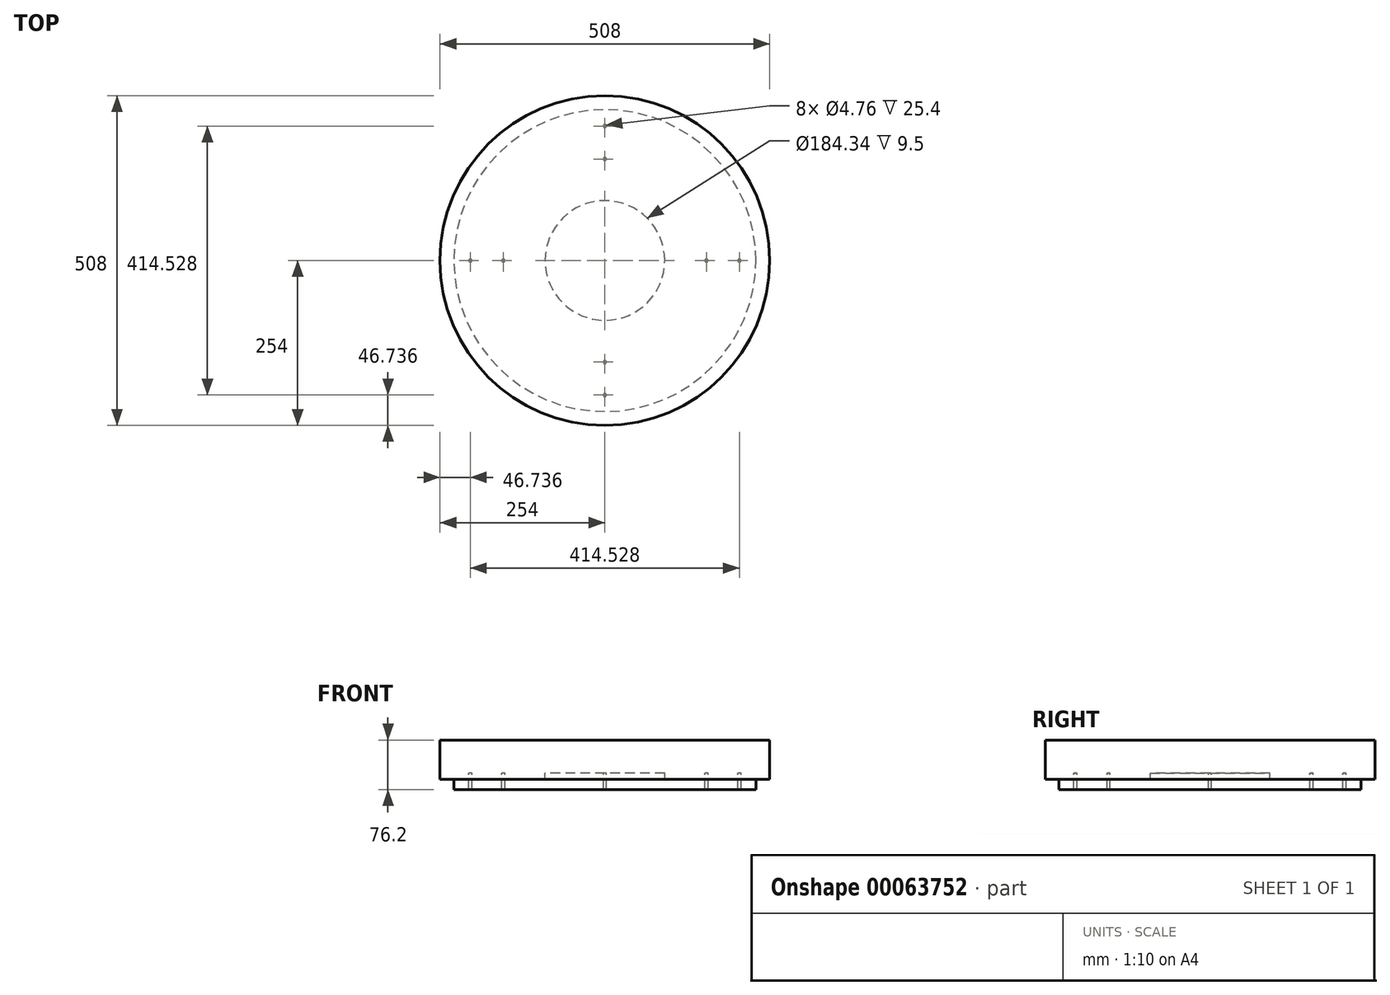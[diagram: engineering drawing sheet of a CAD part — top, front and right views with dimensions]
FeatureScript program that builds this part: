
annotation { "Feature Type Name" : "Feature", "Feature Type Description" : "" }
export const myFeature = defineFeature(function(context is Context, id is Id, definition is map)
    precondition{}
    {
        {
            assignVariable(context, id + "F0", {"name" : "H", "anyValue" : 15});
        }
        {
            assignVariable(context, id + "F1", {"name" : "S", "anyValue" : 4});
        }
        {
            var Q0;
            Q0=qCreatedBy(makeId("Top.planeOp"),FACE);
            var sketch = newSketch(context, id + "F2", { "sketchPlane" : qUnion([Q0])});
            skCircle(sketch, "E0", {"center": v(0, 0) * mm, "radius": 254 * mm});
            skCircle(sketch, "E1", {"center": v(0, 0) * mm, "radius": 241.3 * mm});
            skCircle(sketch, "E2.0", {"center": v(0, 0) * mm, "radius": 232.66 * mm});
            skSolve(sketch);
        }
        {
            var Q0;
            Q0=makeQuery(id+"F2.imprint","IMPRINT",FACE,{"disambiguationData":[TD([[makeQuery(id+"F2.imprint","IMPRINT",EDGE,{"derivedFrom":sQuery(id+"F2.wireOp",EDGE,"E1")}),1.0]])]});
            var Q1;
            Q1=sQuery(id+"F2.wireOp",EDGE,"E1");
            var Q2;
            Q2=sQuery(id+"F2.wireOp",EDGE,"E2.0");
            extrude(context, id + "F3", {"entities" : qUnion([Q0]), "surfaceEntities" : qUnion([Q1, Q2]), "depth" : (getVariable(context, 'H') - 5.5) * mm});
        }
        {
            var Q0;
            Q0=makeQuery(id+"F3.opExtrude","CAP_FACE",FACE,{"disambiguationData":[OSD([sQuery(id+"F2.wireOp",EDGE,"E1"),sQuery(id+"F2.wireOp",EDGE,"E2.0")])],"isStart":false});
            var sketch = newSketch(context, id + "F4", { "sketchPlane" : qUnion([Q0])});
            skCircle(sketch, "E3.0", {"center": v(0, 0) * mm, "radius": 232.66 * mm});
            skSolve(sketch);
        }
        {
            var Q0;
            Q0=qSketchRegion(id+"F4",true);
            extrude(context, id + "F5", {"entities" : qUnion([Q0]), "oppositeDirection" : true, "depth" : 25.4 * mm});
        }
        {
            var Q0;
            Q0=makeQuery(id+"F5.opExtrude","CAP_FACE",FACE,{"disambiguationData":[OSD([sQuery(id+"F4.wireOp",EDGE,"E3.0")])],"isStart":true});
            var sketch = newSketch(context, id + "F6", { "sketchPlane" : qUnion([Q0])});
            skLineSegment(sketch, "E4", {"start": v(-232.66, 0) * mm, "end": v(0, 0) * mm, "construction": true});
            skCircle(sketch, "E5.0", {"center": v(0, 0) * mm, "radius": 207.26 * mm, "construction": true});
            skCircle(sketch, "E6.0", {"center": v(0, 0) * mm, "radius": 156.46 * mm, "construction": true});
            skPoint(sketch, "E7", {"position": v(-207.26, 0) * mm});
            skPoint(sketch, "E8", {"position": v(-156.46, 0) * mm});
            skPoint(sketch, "E9.1.0", {"position": v(0, -156.46) * mm});
            skPoint(sketch, "E9.1.1", {"position": v(0, -207.26) * mm});
            skPoint(sketch, "E9.2.0", {"position": v(156.46, 0) * mm});
            skPoint(sketch, "E9.2.1", {"position": v(207.26, 0) * mm});
            skPoint(sketch, "E9.3.0", {"position": v(0, 156.46) * mm});
            skPoint(sketch, "E9.3.1", {"position": v(0, 207.26) * mm});
            skSolve(sketch);
        }
        {
            var Q0;
            Q0=sQuery(id+"F6.wireOp",VERTEX,"E7");
            var Q1;
            Q1=sQuery(id+"F6.wireOp",VERTEX,"E8");
            var Q2;
            Q2=sQuery(id+"F6.wireOp",VERTEX,"E9.4.1");
            var Q3;
            Q3=sQuery(id+"F6.wireOp",VERTEX,"E9.4.0");
            var Q4;
            Q4=sQuery(id+"F6.wireOp",VERTEX,"E9.3.0");
            var Q5;
            Q5=sQuery(id+"F6.wireOp",VERTEX,"E9.3.1");
            var Q6;
            Q6=sQuery(id+"F6.wireOp",VERTEX,"E9.2.0");
            var Q7;
            Q7=sQuery(id+"F6.wireOp",VERTEX,"E9.2.1");
            var Q8;
            Q8=sQuery(id+"F6.wireOp",VERTEX,"E9.1.1");
            var Q9;
            Q9=sQuery(id+"F6.wireOp",VERTEX,"E9.1.0");
            var Q10;
            Q10=sQuery(id+"F6.wireOp",VERTEX,"58d6160c-07d9-473b-a502-2546abea6cd9.1.6.0");
            var Q11;
            Q11=sQuery(id+"F6.wireOp",VERTEX,"58d6160c-07d9-473b-a502-2546abea6cd9.0.6.0");
            var Q12;
            Q12=sQuery(id+"F6.wireOp",VERTEX,"58d6160c-07d9-473b-a502-2546abea6cd9.0.5.0");
            var Q13;
            Q13=sQuery(id+"F6.wireOp",VERTEX,"58d6160c-07d9-473b-a502-2546abea6cd9.1.5.0");
            var Q14;
            Q14=makeQuery(id+"F5.opExtrude","SWEPT_BODY",BODY,{"disambiguationData":[OSD([sQuery(id+"F4.wireOp",EDGE,"E3.0")])]});
            hole(context, id + "F7", {"style" : HoleStyle.C_SINK, "holeDiameter" : 4.76 * mm, "cSinkDiameter" : 8.43 * mm, "endStyle" : HoleEndStyle.THROUGH, "locations" : qUnion([Q0, Q1, Q2, Q3, Q4, Q5, Q6, Q7, Q8, Q9, Q10, Q11, Q12, Q13]), "scope" : qUnion([Q14]), "cSinkAngle" : 90 * degree});
        }
        {
            var Q0;
            Q0=makeQuery(id+"F5.opExtrude","SWEPT_BODY",BODY,{"disambiguationData":[OSD([sQuery(id+"F4.wireOp",EDGE,"E3.0")])]});
            var Q1;
            Q1=qCreatedBy(makeId("Top.planeOp"),FACE);
            mirror(context, id + "F8", {"entities" : qUnion([Q0]), "mirrorPlane" : qUnion([Q1])});
        }
        {
            var Q0;
            Q0=makeQuery(id+"F8.opPattern","COPY",BODY,{"derivedFrom":makeQuery(id+"F5.opExtrude","SWEPT_BODY",BODY,{"disambiguationData":[OSD([sQuery(id+"F4.wireOp",EDGE,"E3.0")])]}),"instanceName":"1"});
            var Q1;
            Q1=makeQuery(id+"F5.opExtrude","CAP_FACE",FACE,{"disambiguationData":[OSD([sQuery(id+"F4.wireOp",EDGE,"E3.0")])],"isStart":true});
            transform(context, id + "F9", {"entities" : qUnion([Q0]), "transformType" : TransformType.TRANSLATION_3D, "dx" : 0 * mm, "dy" : 0 * mm, "dz" : (getVariable(context, 'H') - 5.5) * mm, "makeCopy" : false});
        }
        {
            var Q0;
            Q0=makeQuery(id+"F8.opPattern","COPY",FACE,{"derivedFrom":makeQuery(id+"F5.opExtrude","CAP_FACE",FACE,{"disambiguationData":[OSD([sQuery(id+"F4.wireOp",EDGE,"E3.0")])],"isStart":true}),"instanceName":"1"});
            var sketch = newSketch(context, id + "F10", { "sketchPlane" : qUnion([Q0])});
            skCircle(sketch, "E10.0", {"center": v(0, 0) * mm, "radius": 214.4 * mm, "construction": true});
            skCircle(sketch, "E11.0", {"center": v(0, 0) * mm, "radius": 177.9 * mm, "construction": true});
            skCircle(sketch, "E12.0", {"center": v(0, 0) * mm, "radius": 141.38 * mm, "construction": true});
            skLineSegment(sketch, "E13", {"start": v(0, 0) * mm, "end": v(0, 214.4) * mm, "construction": true});
            skLineSegment(sketch, "E14.0", {"start": v(22.23, 0) * mm, "end": v(22.23, 265.2) * mm, "construction": true});
            skLineSegment(sketch, "E15.0", {"start": v(-22.23, 0) * mm, "end": v(-22.23, 265.2) * mm, "construction": true});
            skPoint(sketch, "E16", {"position": v(-22.23, 176.5) * mm});
            skPoint(sketch, "E17", {"position": v(-22.23, 139.62) * mm});
            skPoint(sketch, "E18", {"position": v(22.23, 139.62) * mm});
            skPoint(sketch, "E19", {"position": v(22.23, 176.5) * mm});
            skPoint(sketch, "E20", {"position": v(22.23, 213.25) * mm});
            skPoint(sketch, "E21", {"position": v(-22.23, 213.25) * mm});
            skPoint(sketch, "E22.1.0", {"position": v(-139.66, 22) * mm});
            skPoint(sketch, "E22.1.1", {"position": v(-174.73, 33.4) * mm});
            skPoint(sketch, "E22.1.2", {"position": v(-209.68, 44.76) * mm});
            skPoint(sketch, "E22.1.3", {"position": v(-195.95, 87.04) * mm});
            skPoint(sketch, "E22.1.4", {"position": v(-161, 75.68) * mm});
            skPoint(sketch, "E22.1.5", {"position": v(-125.92, 64.28) * mm});
            skPoint(sketch, "E22.2.0", {"position": v(-64.09, -126.02) * mm});
            skPoint(sketch, "E22.2.1", {"position": v(-85.76, -155.86) * mm});
            skPoint(sketch, "E22.2.2", {"position": v(-107.37, -185.59) * mm});
            skPoint(sketch, "E22.2.3", {"position": v(-143.33, -159.46) * mm});
            skPoint(sketch, "E22.2.4", {"position": v(-121.73, -129.73) * mm});
            skPoint(sketch, "E22.2.5", {"position": v(-100.05, -99.9) * mm});
            skPoint(sketch, "E22.3.0", {"position": v(100.05, -99.9) * mm});
            skPoint(sketch, "E22.3.1", {"position": v(121.73, -129.73) * mm});
            skPoint(sketch, "E22.3.2", {"position": v(143.33, -159.46) * mm});
            skPoint(sketch, "E22.3.3", {"position": v(107.37, -185.59) * mm});
            skPoint(sketch, "E22.3.4", {"position": v(85.76, -155.86) * mm});
            skPoint(sketch, "E22.3.5", {"position": v(64.09, -126.02) * mm});
            skPoint(sketch, "E22.4.0", {"position": v(125.92, 64.28) * mm});
            skPoint(sketch, "E22.4.1", {"position": v(161, 75.68) * mm});
            skPoint(sketch, "E22.4.2", {"position": v(195.95, 87.04) * mm});
            skPoint(sketch, "E22.4.3", {"position": v(209.68, 44.76) * mm});
            skPoint(sketch, "E22.4.4", {"position": v(174.73, 33.4) * mm});
            skPoint(sketch, "E22.4.5", {"position": v(139.66, 22) * mm});
            skSolve(sketch);
        }
        {
            var Q0;
            Q0=sQuery(id+"F10.wireOp",VERTEX,"E21");
            var Q1;
            Q1=sQuery(id+"F10.wireOp",VERTEX,"E16");
            var Q2;
            Q2=sQuery(id+"F10.wireOp",VERTEX,"E17");
            var Q3;
            Q3=sQuery(id+"F10.wireOp",VERTEX,"E18");
            var Q4;
            Q4=sQuery(id+"F10.wireOp",VERTEX,"E19");
            var Q5;
            Q5=sQuery(id+"F10.wireOp",VERTEX,"E20");
            var Q6;
            Q6=sQuery(id+"F10.wireOp",VERTEX,"E22.4.0");
            var Q7;
            Q7=sQuery(id+"F10.wireOp",VERTEX,"E22.4.1");
            var Q8;
            Q8=sQuery(id+"F10.wireOp",VERTEX,"E22.4.2");
            var Q9;
            Q9=sQuery(id+"F10.wireOp",VERTEX,"E22.4.3");
            var Q10;
            Q10=sQuery(id+"F10.wireOp",VERTEX,"E22.4.4");
            var Q11;
            Q11=sQuery(id+"F10.wireOp",VERTEX,"E22.4.5");
            var Q12;
            Q12=sQuery(id+"F10.wireOp",VERTEX,"E22.3.0");
            var Q13;
            Q13=sQuery(id+"F10.wireOp",VERTEX,"E22.3.1");
            var Q14;
            Q14=sQuery(id+"F10.wireOp",VERTEX,"E22.3.2");
            var Q15;
            Q15=sQuery(id+"F10.wireOp",VERTEX,"E22.3.3");
            var Q16;
            Q16=sQuery(id+"F10.wireOp",VERTEX,"E22.3.4");
            var Q17;
            Q17=sQuery(id+"F10.wireOp",VERTEX,"E22.3.5");
            var Q18;
            Q18=sQuery(id+"F10.wireOp",VERTEX,"E22.2.2");
            var Q19;
            Q19=sQuery(id+"F10.wireOp",VERTEX,"E22.2.1");
            var Q20;
            Q20=sQuery(id+"F10.wireOp",VERTEX,"E22.2.0");
            var Q21;
            Q21=sQuery(id+"F10.wireOp",VERTEX,"E22.2.5");
            var Q22;
            Q22=sQuery(id+"F10.wireOp",VERTEX,"E22.2.4");
            var Q23;
            Q23=sQuery(id+"F10.wireOp",VERTEX,"E22.2.3");
            var Q24;
            Q24=sQuery(id+"F10.wireOp",VERTEX,"E22.1.0");
            var Q25;
            Q25=sQuery(id+"F10.wireOp",VERTEX,"E22.1.5");
            var Q26;
            Q26=sQuery(id+"F10.wireOp",VERTEX,"E22.1.1");
            var Q27;
            Q27=sQuery(id+"F10.wireOp",VERTEX,"E22.1.2");
            var Q28;
            Q28=sQuery(id+"F10.wireOp",VERTEX,"E22.1.3");
            var Q29;
            Q29=sQuery(id+"F10.wireOp",VERTEX,"E22.1.4");
            var Q30;
            Q30=makeQuery(id+"F8.opPattern","COPY",BODY,{"derivedFrom":makeQuery(id+"F5.opExtrude","SWEPT_BODY",BODY,{"disambiguationData":[OSD([sQuery(id+"F4.wireOp",EDGE,"E3.0")])]}),"instanceName":"1"});
            hole(context, id + "F11", {"style" : HoleStyle.SIMPLE, "holeDiameter" : 3.17 * mm, "endStyle" : HoleEndStyle.BLIND, "holeDepth" : 3.17 * mm, "locations" : qUnion([Q0, Q1, Q2, Q3, Q4, Q5, Q6, Q7, Q8, Q9, Q10, Q11, Q12, Q13, Q14, Q15, Q16, Q17, Q18, Q19, Q20, Q21, Q22, Q23, Q24, Q25, Q26, Q27, Q28, Q29]), "scope" : qUnion([Q30])});
        }
        {
            var Q0;
            Q0=makeQuery(id+"F8.opPattern","COPY",FACE,{"derivedFrom":makeQuery(id+"F5.opExtrude","CAP_FACE",FACE,{"disambiguationData":[OSD([sQuery(id+"F4.wireOp",EDGE,"E3.0")])],"isStart":false}),"instanceName":"1"});
            var sketch = newSketch(context, id + "F12", { "sketchPlane" : qUnion([Q0])});
            skCircle(sketch, "E23", {"center": v(0, 0) * mm, "radius": 92.17 * mm});
            skSolve(sketch);
        }
        {
            var Q0;
            Q0=qSketchRegion(id+"F12",true);
            extrude(context, id + "F13", {"entities" : qUnion([Q0]), "operationType" : NewBodyOperationType.REMOVE, "oppositeDirection" : true, "depth" : 25.4 * mm});
        }
        {
            var Q0;
            Q0=makeQuery(id+"F8.opPattern","COPY",FACE,{"derivedFrom":makeQuery(id+"F5.opExtrude","CAP_FACE",FACE,{"disambiguationData":[OSD([sQuery(id+"F4.wireOp",EDGE,"E3.0")])],"isStart":false}),"instanceName":"1"});
            var sketch = newSketch(context, id + "F14", { "sketchPlane" : qUnion([Q0])});
            skLineSegment(sketch, "E24", {"start": v(-207.26, 0) * mm, "end": v(-156.46, 0) * mm, "construction": true});
            skLineSegment(sketch, "E25.0", {"start": v(-232.66, 12.7) * mm, "end": v(-131.06, 12.7) * mm});
            skLineSegment(sketch, "E26.0", {"start": v(-232.66, -12.7) * mm, "end": v(-131.06, -12.7) * mm});
            skLineSegment(sketch, "E27", {"start": v(-232.66, -12.7) * mm, "end": v(-232.66, 12.7) * mm});
            skLineSegment(sketch, "E28", {"start": v(-131.06, -12.7) * mm, "end": v(-131.06, 12.7) * mm});
            skSolve(sketch);
        }
        {
            var Q0;
            Q0=qSketchRegion(id+"F14",true);
            extrude(context, id + "F15", {"entities" : qUnion([Q0]), "depth" : (getVariable(context, 'H') - 7.5) * mm});
        }
        {
            var Q0;
            Q0=makeQuery(id+"F15.opExtrude","SWEPT_BODY",BODY,{"disambiguationData":[OSD([sQuery(id+"F14.wireOp",EDGE,"E25.0"),sQuery(id+"F14.wireOp",EDGE,"E26.0"),sQuery(id+"F14.wireOp",EDGE,"E27"),sQuery(id+"F14.wireOp",EDGE,"E28")])]});
            var Q1;
            Q1=makeQuery(id+"F8.opPattern","COPY",EDGE,{"derivedFrom":makeQuery(id+"F5.opExtrude","CAP_EDGE",EDGE,{"disambiguationData":[OSD([sQuery(id+"F4.wireOp",EDGE,"E3.0")])],"isStart":false}),"instanceName":"1"});
            circularPattern(context, id + "F16", {"entities" : qUnion([Q0]), "axis" : qUnion([Q1]), "angle" : 360 * degree, "instanceCount" : round(getVariable(context, 'S')), "equalSpace" : true});
        }
        {
            var Q0;
            Q0=makeQuery(id+"F2.imprint","IMPRINT",FACE,{"disambiguationData":[TD([[makeQuery(id+"F2.imprint","IMPRINT",EDGE,{"derivedFrom":sQuery(id+"F2.wireOp",EDGE,"E0")}),1.0]])]});
            extrude(context, id + "F17", {"entities" : qUnion([Q0]), "depth" : (getVariable(context, 'H') - 5.5) * mm});
        }
        {
            var Q0;
            Q0=makeQuery(id+"F17.opExtrude","CAP_FACE",FACE,{"disambiguationData":[OSD([sQuery(id+"F2.wireOp",EDGE,"E0"),sQuery(id+"F2.wireOp",EDGE,"E1")])],"isStart":false});
            var sketch = newSketch(context, id + "F18", { "sketchPlane" : qUnion([Q0])});
            skCircle(sketch, "E29.0", {"center": v(0, 0) * mm, "radius": 254 * mm});
            skSolve(sketch);
        }
        {
            var Q0;
            Q0=qSketchRegion(id+"F18",true);
            extrude(context, id + "F19", {"entities" : qUnion([Q0]), "operationType" : NewBodyOperationType.ADD, "depth" : 50.8 * mm});
        }
    });
